# Revit family: QF_ELECTROLUXPROFESSIONAL_1LSN96_WH6-27_E
name_source: partatom
category: Attrezzature speciali
units: mm (PartAtom-declared; Revit-internal decimal feet)

## family parameters
Basato su piano di lavoro = No
Condiviso = No
Punto di calcolo locali = No
Quota connettore circolare = Usa diametro
Sempre verticale = Sì
Taglio con vuoti quando caricato = No
Tipo di parte = Normale

## types (47) — shared parameters
Depth Actual = 990 mm  [stored 3.24803 ft]
Height Actual = 1462 mm  [stored 4.79659 ft]
Latent Heat Output = 0.0
Length Actual = 1020 mm  [stored 3.34646 ft]
Modello = WH6-27
Produttore = Electrolux Professional
Sensible Heat Output = 0.0
URL = www.electroluxprofessional.com
Weight = 425
zero-valued in all types: Gas KW, Prospetto di default, Steam Pounds per Hour

## per-type parameters (varying)
| type | Cycle | Descrizione | Item Number | Phase | Volts | Watts |
| 9868130338 | 50 Hz | WASHER WH6-27 27KG EL 19,8KW 415/50/3N COMPASS PRO 6G01 ML 2xWATER POWDER+5xLIQ. VALV.CLOSED SST/SILVER 2.I/O DISCON. ST | 1LM0B9 | 3 | 415 V | 20500 W |
| 9868130129 | 50 Hz | WASHER WH6-27 27KG EL 19,8KW 415/50/3N COMPASS PRO 6H01 ML 2xWATER POWDER+5xLIQ. EL.VALV.OPEN SST/SILVER 2.I/O DISCON. S | 1LSP65 | 3 | 415 V | 20500 W |
| 9868130166 | 50 Hz | WASHER WH6-27 27KG MOP 23KW 380-400/220-230/50/3N/3 COMPASS PRO 6M17 ML 2xWATER POWDER+5xLIQ. EL.VALV.CLOSED SILVER 2.I/ | 1L0GAL | 3 | 400 V | 19900 W |
| 9868130345 | 60 Hz | WASHER WH6-27 27KG EL 22,8KW 480/60/3 COMPASS PRO 6G01 ML 2xWATER POWDER+5xLIQ. EL.VALV.OPEN SST/SILVER 2.I/O TRAFO DISC | 1L0HDU | 3 | 480 V | 23500 W |
| 9868130169 | 50 Hz | WASHER WH6-27 27KG EL 19,1KW 380-400/220-230/50/3N/3 COMPASS PRO 6H12 ML 2xWATER POWDER+5xLIQ. VALV.OPEN SILVER 2.I/O QC | 1L0GBT | 3 | 400 V | 19900 W |
| 9868130149 | 50 Hz | WASHER WH6-27 27KG EL 19,1KW 380-400/220-230/50/3N/3 COMPASS PRO 6G01 ML 2xWATER POWDER+5xLIQ. VALV.OPEN SILVER 2.I/O DI | 1L8229 | 3 | 400 V | 19900 W |
| 9868130131 | 50 Hz | WASHER WH6-27 27KG EL 19,1KW 380-400/50/3N COMPASS PRO 6G01 CH-EN 2xWATER POWDER+5xLIQ. VALV.OPEN SST/SILVER 2.I/O DISCO | 1L0HG7 | 3 | 400 V | 19800 W |
| 9868130156 | 50 Hz | WASHER WH6-27 27KG EL 19,1KW 380-400/50/3N COMPASS PRO 6G01 CH-EN 2xWATER POWDER+5xLIQ. VALV.OPEN SILVER 2.I/O DISCON. S | 1L822G | 3 | 400 V | 19800 W |
| 9868130261 | 50 Hz | WASHER WH6-27 27KG NO HEAT 220-240/50/1N COMPASS PRO 6G01 CH-EN 2xWATER POWDER VALV.OPEN SILVER DISCON. STOP | 1LA232 | 1 | 240 V | 2700 W |
| 9868130310 | 50 Hz | WASHER WH6-27 27KG NO HEAT 220-240/50/1N COMPASS PRO 6L07 ML 2xWATER 5xLIQ. VALV.OPEN SILVER 2.I/O DISCON. | 1LSPRM | 1 | 240 V | 2600 W |
| 9868130293 | 50 Hz | WASHER WH6-27 27KG EL 19,1KW 380-400/220-230/50/3N/3 COMPASS PRO 6B01 ML 2xWATER POWDER+5xLIQ. VALV.OPEN SST/SILVER 2.I/ | 1L0GZT | 3 | 400 V | 19900 W |
| 9868130184 | 50 Hz | WASHER WH6-27 27KG EL 19,1KW 380-400/50/3N COMPASS PRO 6H12 SE 2xWATER POWDER+5xLIQ. VALV.OPEN SILVER 2.I/O QC DISCON. S | 1LA1A2 | 3 | 400 V | 19800 W |
| 9868130337 | 50 Hz | WASHER WH6-27 27KG EL 19,8KW 415/50/3N COMPASS PRO 6G01 ML 2xWATER POWDER+5xLIQ. VALV.CLOSED SILVER 2.I/O DISCON. STOP | 1LM0B8 | 3 | 415 V | 20500 W |
| 9868130253 | 50 Hz | WASHER WH6-27 27KG NO HEAT 220-240/50/1N COMPASS PRO 6G01 ML 2xWATER POWDER+5xLIQ. VALV.OPEN SILVER 2.I/O DISCON. STOP | 1L0GRX | 1 | 240 V | 2700 W |
| 9868130357 | 50 Hz | WASHER WH6-27 27KG EL 21KW 440/50/3 COMPASS PRO 6G01 ML 2xWATER POWDER+5xLIQ. VALV.OPEN SST/SILVER 2.I/O TRAFO DISCON. S | 1L0HEJ | 3 | 440 V | 21700 W |
| 9868130154 | 50 Hz | WASHER WH6-27 27KG EL 19,8KW 415/50/3N COMPASS PRO 6H01 ML 2xWATER POWDER+5xLIQ. EL.VALV.OPEN SILVER 2.I/O DISCON. STOP | 1L822E | 3 | 415 V | 20500 W |
| 9868130127 | 50 Hz | WASHER WH6-27 27KG NO HEAT 200/50/60/3 COMPASS PRO 6H42 JP,EN 2xWATER POWDER+5xLIQ. VALV.OPEN SST/SILVER 2.I/O DISCON. | 1LA1BP | 3 | 200 V | 2600 W |
| 9868130003 | 50 Hz | WH6-27 SG/SG/BL 19,1 EX 8G01 | 1L0EZD | 3 | 400 V | 19800 W |
| 9868130117 | 50 Hz | WASHER WH6-27 27KG EL 19,8KW 415/50/3N COMPASS PRO 6G01 ML 2xWATER POWDER+5xLIQ. VALV.OPEN SST/SILVER 2.I/O DISCON. STOP | 1L8265 | 3 | 415 V | 20500 W |
| 9868130250 | 50 Hz | WASHER WH6-27 27KG EL 14,4KW 200/50/60/3 COMPASS PRO 6H43 JP,EN 2xWATER POWDER+5xLIQ. VALV.OPEN SILVER 2.I/O DISCON. | 1L0GRM | 3 | 200 V | 15100 W |
| 9868130309 | 50 Hz | WASHER WH6-27 27KG NO HEAT 220-240/50/1N COMPASS PRO 6L01 ML 2xWATER 5xLIQ. VALV.OPEN SILVER 2.I/O DISCON. | 1LSPRL | 1 | 240 V | 2600 W |
| 9868130321 | 60 Hz | WASHER WH6-27 27KG EL 19,8KW 208-240/60/3 COMPASS PRO 6G01 ML 2xWATER POWDER+5xLIQ. EL.VALV.OPEN SST/SILVER 2.I/O DISCON | 1L0H2X | 3 | 240 V | 20500 W |
| 9868130089 | 50 Hz | WASHER WH6-27 27KG EL 19,1KW 380-400/50/3N COMPASS PRO 6G01 ML 2xWATER POWDER+5xLIQ. VALV.OPEN SILVER 2.I/O DISCON. STOP | 1L824L | 3 | 400 V | 19800 W |
| 9868130152 | 50 Hz | WASHER WH6-27 27KG NO HEAT 200/50/60/3 COMPASS PRO 6H42 JP,EN 2xWATER POWDER+5xLIQ. VALV.OPEN SILVER 2.I/O DISCON. | 1L822C | 3 | 200 V | 2600 W |
| 9868130341 | 50 Hz | WASHER WH6-27 27KG EL 19,8KW 240/50/3 COMPASS PRO 6G01 ML 2xWATER POWDER+5xLIQ. VALV.OPEN SST/SILVER 2.I/O DISCON. STOP | 1LM0BM | 3 | 240 V | 20500 W |
| 9868130004 | 50 Hz | WH6-27 SG/SG/BL 19,1 EX 8G01 | 1L0EZE | 3 | 400 V | 19800 W |
| 9868130292 | 50 Hz | WASHER WH6-27 27KG MOP 23KW 240/50/3 COMPASS PRO 6M14 ML 2xWATER POWDER+5xLIQ. EL.VALV.OPEN SILVER 2.I/O QC DISCON. STOP | 1L0GZJ | 3 | 240 V | 23700 W |
| 9868130009 | 60 Hz | WH6-27 SG/SG HW EXUS 8Lxx | 1L0EZK | 1 | 240 V | 2700 W |
| 9868130185 | 50 Hz | WASHER WH6-27 27KG MOP 23KW 380-400/220-230/50/3N/3 COMPASS PRO 6M14 SE 2xWATER POWDER+5xLIQ. EL.VALV.OPEN SILVER 2.I/O | 1LA1A3 | 3 | 400 V | 19900 W |
| 9868130195 | 50 Hz | WASHER WH6-27 27KG NO HEAT 220-240/50/1N COMPASS PRO 6L01 ML 2xWATER POWDER+5xLIQ. VALV.OPEN SST/SILVER EXT.PM. 2.I/O DI | 1LSP9P | 1 | 240 V | 2700 W |
| 9868130245 | 60 Hz | WASHER WH6-27 27KG NO HEAT 208-240/60/1 COMPASS PRO 6L01 ML 2xWATER POWDER+5xLIQ. VALV.OPEN SILVER ELS-NETW. 2.I/O | 1L0GP3 | 1 | 240 V | 2700 W |
| 9868130212 | 60 Hz | WASHER WH6-27 27KG EL 19,1KW 380-400/60/3 COMPASS PRO 6G01 ML 2xWATER POWDER+5xLIQ. VALV.OPEN SILVER 2.I/O TRAFO DISCON. | 1L0GF0 | 3 | 400 V | 19800 W |
| 9868130128 | 50 Hz | WASHER WH6-27 27KG EL 19,1KW 380-400/50/3N COMPASS PRO 6G01 ML 2xWATER POWDER VALV.OPEN SST/SILVER DISCON. STOP | 1LSP64 | 3 | 400 V | 19800 W |
| 9868130155 | 50 Hz | WASHER WH6-27 27KG EL 19,8KW 415/50/3N COMPASS PRO 6H01 ML 2xWATER POWDER+5xLIQ. VALV.OPEN SILVER 2.I/O DISCON. STOP | 1L822F | 3 | 415 V | 20500 W |
| 9868130354 | 60 Hz | WASHER WH6-27 27KG NO HEAT 208-240/60/1 COMPASS PRO 6G01 ML 2xWATER POWDER+5xLIQ. VALV.OPEN SILVER 2.I/O STOP | 1L0HE5 | 1 | 240 V | 2700 W |
| 9868130148 | 50 Hz | WASHER WH6-27 27KG EL 19,8KW 415/50/3N COMPASS PRO 6G01 ML 2xWATER POWDER+5xLIQ. VALV.OPEN SILVER 2.I/O DISCON. STOP | 1L8228 | 3 | 415 V | 20500 W |
| 9868130130 | 50 Hz | WASHER WH6-27 27KG EL 19,8KW 415/50/3N COMPASS PRO 6H01 ML 2xWATER POWDER+5xLIQ. VALV.OPEN SST/SILVER 2.I/O DISCON. STOP | 1LSP66 | 3 | 415 V | 20500 W |
| 9868130170 | 50 Hz | WASHER WH6-27 27KG MOP 23KW 380-400/220-230/50/3N/3 COMPASS PRO 6M14 ML 2xWATER POWDER+5xLIQ. EL.VALV.OPEN SILVER 2.I/O | 1L0GBU | 3 | 400 V | 19900 W |
| 9868130082 | 50 Hz | WASHER WH6-27 27KG EL 19,1KW 380-400/50/3N COMPASS PRO 6G01 ML 2xWATER POWDER+5xLIQ. VALV.OPEN SST/SILVER 2.I/O DISCON. | 1LSPAT | 3 | 400 V | 19800 W |
| 9868130002 | 50 Hz | WH6-27 SG/SG/BL 19,1 EX 8G01 | 1L0EZC | 3 | 400 V | 198000 W |
| 9868130336 | 50 Hz | WASHER WH6-27 27KG EL 19,1KW 380-400/50/3N COMPASS PRO 6G01 ML 2xWATER POWDER+5xLIQ. VALV.OPEN SST 2.I/O DISCON. STOP | 1LM0AV | 3 | 400 V | 19800 W |
| 9868130123 | 50 Hz | WASHER WH6-27 27KG EL 19,1KW 380-400/220-230/50/3N/3 COMPASS PRO 6G01 ML 2xWATER POWDER+5xLIQ. VALV.OPEN SST/SILVER 2.I/ | 1L0GPJ | 3 | 400 V | 19900 W |
| 9868130173 | 50 Hz | WASHER WH6-27 27KG MOP 23KW 380-400/220-230/50/3N/3 COMPASS PRO 6M16 ML 2xWATER POWDER+5xLIQ. EL.VALV.CLOSED SILVER 2.I/ | 1L0GBX | 3 | 400 V | 19900 W |
| 9868130366 | 60 Hz | WASHER WH6-27 27KG EL 19,1KW 380-400/60/3 COMPASS PRO 6G07 ML 2xWATER POWDER+5xLIQ. VALV.OPEN SILVER 2.I/O TRAFO DISCON. | 1LT6EN | 3 | 400 V | 19800 W |
| 9868130346 | 50 Hz | WASHER WH6-27 27KG EL 21KW 440/50/3 COMPASS PRO 6G01 ML 2xWATER POWDER+5xLIQ. VALV.CLOSED SILVER 2.I/O TRAFO DISCON. STO | 1L0HDV | 3 | 440 V | 21700 W |
| 9868130153 | 50 Hz | WASHER WH6-27 27KG EL 19,1KW 380-400/50/3N COMPASS PRO 6G01 ML 2xWATER POWDER VALV.OPEN SILVER DISCON. STOP | 1L822D | 3 | 400 V | 19800 W |
| 9868130196 | 60 Hz | WASHER WH6-27 27KG EL 21KW 440/60/3 COMPASS PRO 6G01 ML 2xWATER POWDER+5xLIQ. EL.VALV.OPEN SST/SILVER 2.I/O TRAFO DISCON | 1LSPAU | 3 | 440 V | 21700 W |

note: [stored X ft] marks values corroborated as IEEE doubles in the binary element streams (Revit-internal decimal feet)

## geometry (parser evidence)
native form markers: Blend x8
no freeform markers — native parametric forms only
